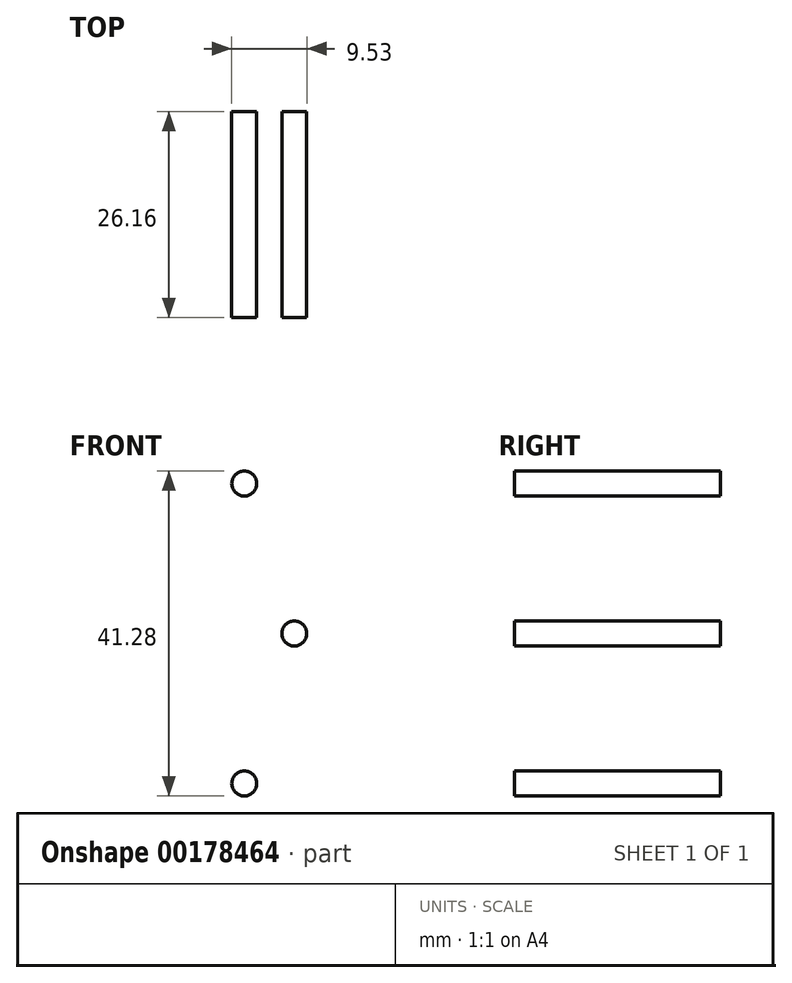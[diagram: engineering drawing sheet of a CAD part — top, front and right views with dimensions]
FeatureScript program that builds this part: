
annotation { "Feature Type Name" : "Feature", "Feature Type Description" : "" }
export const myFeature = defineFeature(function(context is Context, id is Id, definition is map)
    precondition{}
    {
        {
            var Q0;
            Q0=qCreatedBy(makeId("Front.planeOp"),FACE);
            var sketch = newSketch(context, id + "F0", { "sketchPlane" : qUnion([Q0])});
            skLineSegment(sketch, "E0.bottom", {"start": v(527.05, 495.3) * mm, "end": v(-527.05, 495.3) * mm});
            skLineSegment(sketch, "E0.top", {"start": v(527.05, -495.3) * mm, "end": v(-527.05, -495.3) * mm});
            skLineSegment(sketch, "E0.left", {"start": v(527.05, 495.3) * mm, "end": v(527.05, -495.3) * mm});
            skLineSegment(sketch, "E0.right", {"start": v(-527.05, 495.3) * mm, "end": v(-527.05, -495.3) * mm});
            skPoint(sketch, "E0.middle", {"position": v(0, 0) * mm});
            skSolve(sketch);
        }
        {
            var Q0;
            Q0 = qSketchRegion(id + "F0", true);
            extrude(context, id + "F1", {"entities" : qUnion([Q0]), "depth" : 0.76 * mm});
        }
        {
            var Q0;
            Q0=makeQuery(id+"F1.opExtrude","CAP_FACE",FACE,{"disambiguationData":[OSD([sQuery(id+"F0.wireOp",EDGE,"E0.bottom"),sQuery(id+"F0.wireOp",EDGE,"E0.top"),sQuery(id+"F0.wireOp",EDGE,"E0.left"),sQuery(id+"F0.wireOp",EDGE,"E0.right")])],"isStart":false});
            var sketch = newSketch(context, id + "F2", { "sketchPlane" : qUnion([Q0])});
            skLineSegment(sketch, "E1.bottom", {"start": v(527.05, 457.2) * mm, "end": v(-488.95, 457.2) * mm});
            skLineSegment(sketch, "E1.top", {"start": v(527.05, -457.2) * mm, "end": v(-488.95, -457.2) * mm});
            skLineSegment(sketch, "E1.left", {"start": v(527.05, 457.2) * mm, "end": v(527.05, -457.2) * mm});
            skLineSegment(sketch, "E1.right", {"start": v(-488.95, 457.2) * mm, "end": v(-488.95, -457.2) * mm});
            skPoint(sketch, "E1.middle", {"position": v(19.05, 0) * mm});
            skSolve(sketch);
        }
        {
            var Q0;
            Q0 = qSketchRegion(id + "F2", true);
            extrude(context, id + "F3", {"entities" : qUnion([Q0]), "operationType" : NewBodyOperationType.ADD, "depth" : 25.4 * mm});
        }
        {
            var Q0;
            Q0=makeQuery(id+"F1.opExtrude","CAP_FACE",FACE,{"disambiguationData":[OSD([sQuery(id+"F0.wireOp",EDGE,"E0.bottom"),sQuery(id+"F0.wireOp",EDGE,"E0.top"),sQuery(id+"F0.wireOp",EDGE,"E0.left"),sQuery(id+"F0.wireOp",EDGE,"E0.right")])],"isStart":true});
            var sketch = newSketch(context, id + "F4", { "sketchPlane" : qUnion([Q0])});
            skLineSegment(sketch, "E2", {"start": v(-501.65, 495.3) * mm, "end": v(-501.65, -495.3) * mm, "construction": true});
            skLineSegment(sketch, "E3", {"start": v(-501.65, 228.6) * mm, "end": v(-527.05, 228.6) * mm, "construction": true});
            skLineSegment(sketch, "E4", {"start": v(-527.05, 177.8) * mm, "end": v(-501.65, 177.8) * mm, "construction": true});
            skLineSegment(sketch, "E5", {"start": v(-514.35, 228.6) * mm, "end": v(-514.35, 177.8) * mm, "construction": true});
            skLineSegment(sketch, "E6", {"start": v(-520.7, 228.6) * mm, "end": v(-520.7, 177.8) * mm, "construction": true});
            skLineSegment(sketch, "E7", {"start": v(-514.35, 222.25) * mm, "end": v(-527.05, 222.25) * mm, "construction": true});
            skLineSegment(sketch, "E8", {"start": v(-514.35, 184.15) * mm, "end": v(-527.05, 184.15) * mm, "construction": true});
            skLineSegment(sketch, "E9", {"start": v(-514.35, 203.2) * mm, "end": v(-527.05, 203.2) * mm, "construction": true});
            skCircle(sketch, "E10", {"center": v(-520.7, 203.2) * mm, "radius": 1.59 * mm});
            skCircle(sketch, "E11", {"center": v(-514.35, 222.25) * mm, "radius": 1.59 * mm});
            skCircle(sketch, "E12", {"center": v(-514.35, 184.15) * mm, "radius": 1.59 * mm});
            skCircle(sketch, "E13.MirrorC", {"center": v(-520.7, -203.2) * mm, "radius": 1.59 * mm});
            skCircle(sketch, "E14.MirrorC", {"center": v(-514.35, -222.25) * mm, "radius": 1.59 * mm});
            skCircle(sketch, "E15.MirrorC", {"center": v(-514.35, -184.15) * mm, "radius": 1.59 * mm});
            skSolve(sketch);
        }
        {
            var Q0;
            Q0=makeQuery(id+"F4.imprint","IMPRINT",FACE,{"disambiguationData":[TD([[makeQuery(id+"F4.imprint","IMPRINT",EDGE,{"derivedFrom":sQuery(id+"F4.wireOp",EDGE,"E10")}),1.0]])]});
            var Q1;
            Q1=makeQuery(id+"F4.imprint","IMPRINT",FACE,{"disambiguationData":[TD([[makeQuery(id+"F4.imprint","IMPRINT",EDGE,{"derivedFrom":sQuery(id+"F4.wireOp",EDGE,"E11")}),1.0]])]});
            var Q2;
            Q2=makeQuery(id+"F4.imprint","IMPRINT",FACE,{"disambiguationData":[TD([[makeQuery(id+"F4.imprint","IMPRINT",EDGE,{"derivedFrom":sQuery(id+"F4.wireOp",EDGE,"E12")}),1.0]])]});
            var Q3;
            Q3=makeQuery(id+"F4.imprint","IMPRINT",FACE,{"disambiguationData":[TD([[makeQuery(id+"F4.imprint","IMPRINT",EDGE,{"derivedFrom":sQuery(id+"F4.wireOp",EDGE,"E15.MirrorC")}),-1.0]])]});
            var Q4;
            Q4=makeQuery(id+"F4.imprint","IMPRINT",FACE,{"disambiguationData":[TD([[makeQuery(id+"F4.imprint","IMPRINT",EDGE,{"derivedFrom":sQuery(id+"F4.wireOp",EDGE,"E13.MirrorC")}),-1.0]])]});
            var Q5;
            Q5=makeQuery(id+"F4.imprint","IMPRINT",FACE,{"disambiguationData":[TD([[makeQuery(id+"F4.imprint","IMPRINT",EDGE,{"derivedFrom":sQuery(id+"F4.wireOp",EDGE,"E14.MirrorC")}),-1.0]])]});
            extrude(context, id + "F5", {"entities" : qUnion([Q0, Q1, Q2, Q3, Q4, Q5]), "operationType" : NewBodyOperationType.REMOVE, "endBound" : BoundingType.THROUGH_ALL, "oppositeDirection" : true, "depth" : 25.4 * mm});
        }
    });
